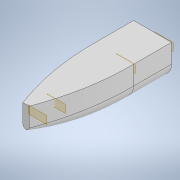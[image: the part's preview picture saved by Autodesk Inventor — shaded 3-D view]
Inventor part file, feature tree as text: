
AUTODESK INVENTOR PART (.ipt)
format: ipt  version: 2020.3 (Build 243373000, 373)  size: 198,144 bytes
history: native  units: mm
features: sketch x4, plane x4, extrude x1, loft x1, projected_geometry x1, other x1
ambient origin geometry x8: Origin, YZ Plane, XZ Plane, XY Plane, X Axis, Y Axis, Z Axis, Center Point
bodies: Solid1 (feature_tree)
feature tree (12):
  sketch  "Sketch1"  dims[d0=60.0mm d1=170.0mm]
  plane  "Work Plane1"
  plane  "Work Plane2"
  plane  "Work Plane3"
  plane  "Work Plane4"
  extrude  "Extrusion1"  Depth=170.0mm
  sketch  "Sketch2"  dims[d2=200.0mm d3=30.0mm]
  loft  "Loft3"
  projected_geometry  "Projected Loop1"
  sketch  "Sketch3"  dims[d4=60.0mm]
  sketch  "Sketch4"  dims[d5=30.0mm d7=18.0mm d8=30.0mm d9=18.0mm d10=30.0mm d11=10.0mm d12=0.0mm d13=30.0mm d14=15.126927mm d16=9.076156mm d17=15.0mm d18=15.0mm d19=9.076156mm d24=10.0mm d25=5.0mm d26=3.0mm d27=3.0mm d28=5.0mm d29=5.0mm d35=0.0mm d36=90.0deg d37=0.0mm d38=90.0deg d39=0.0mm d40=90.0deg]
  other  "Edges3"
